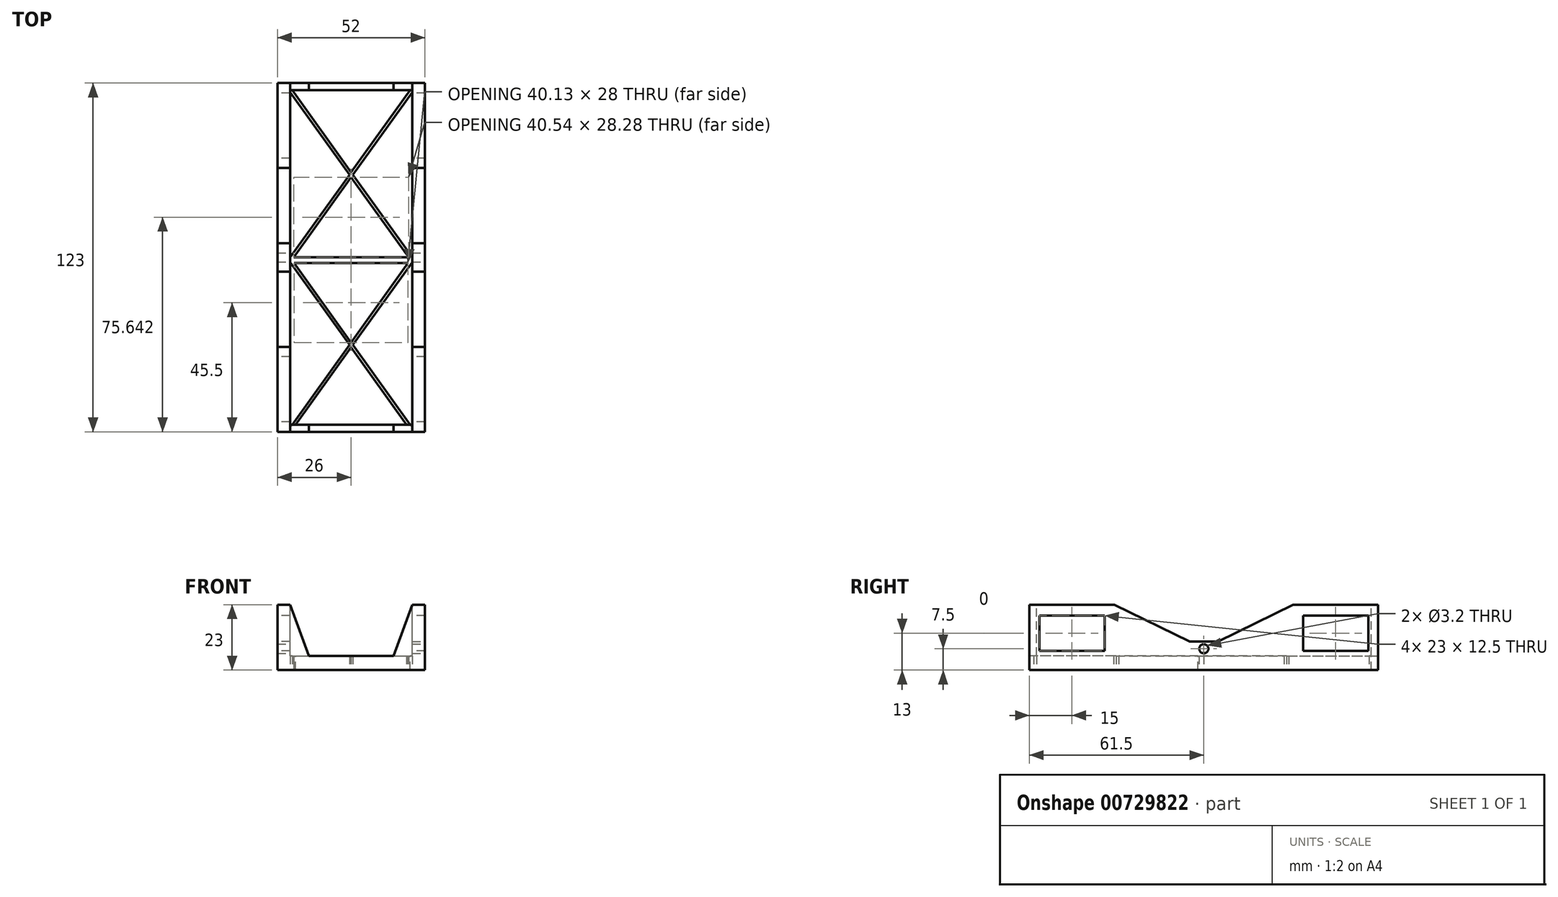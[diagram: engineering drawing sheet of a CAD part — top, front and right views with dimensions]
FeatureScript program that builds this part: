
annotation { "Feature Type Name" : "Feature", "Feature Type Description" : "" }
export const myFeature = defineFeature(function(context is Context, id is Id, definition is map)
    precondition{}
    {
        {
            var Q0;
            Q0=qCreatedBy(makeId("Top.planeOp"),FACE);
            var sketch = newSketch(context, id + "F0", { "sketchPlane" : qUnion([Q0])});
            skLineSegment(sketch, "E0.bottom", {"start": v(21.5, 60) * mm, "end": v(-21.5, 60) * mm});
            skLineSegment(sketch, "E0.top", {"start": v(21.5, -60) * mm, "end": v(-21.5, -60) * mm});
            skLineSegment(sketch, "E0.left", {"start": v(21.5, 60) * mm, "end": v(21.5, -60) * mm});
            skLineSegment(sketch, "E0.right", {"start": v(-21.5, 60) * mm, "end": v(-21.5, -60) * mm});
            skPoint(sketch, "E0.middle", {"position": v(0, 0) * mm});
            skLineSegment(sketch, "E1.bottom", {"start": v(23, 61.5) * mm, "end": v(-23, 61.5) * mm});
            skLineSegment(sketch, "E1.top", {"start": v(23, -61.5) * mm, "end": v(-23, -61.5) * mm});
            skLineSegment(sketch, "E1.left", {"start": v(23, 61.5) * mm, "end": v(23, -61.5) * mm});
            skLineSegment(sketch, "E1.right", {"start": v(-23, 61.5) * mm, "end": v(-23, -61.5) * mm});
            skLineSegment(sketch, "E2", {"start": v(-21.5, 0) * mm, "end": v(21.5, 60) * mm});
            skLineSegment(sketch, "E3", {"start": v(-21.5, 0) * mm, "end": v(21.5, -60) * mm});
            skLineSegment(sketch, "E4", {"start": v(-21.5, -60) * mm, "end": v(21.5, 0) * mm});
            skLineSegment(sketch, "E5", {"start": v(-21.5, 60) * mm, "end": v(21.5, 0) * mm});
            skLineSegment(sketch, "E6", {"start": v(-21.5, 0) * mm, "end": v(21.5, 0) * mm});
            skLineSegment(sketch, "E7.0", {"start": v(-22.31, -0.58) * mm, "end": v(20.69, -60.58) * mm});
            skLineSegment(sketch, "E8.0", {"start": v(-20.69, -60.58) * mm, "end": v(22.31, -0.58) * mm});
            skLineSegment(sketch, "E9.0", {"start": v(-21.5, -1) * mm, "end": v(21.5, -1) * mm});
            skLineSegment(sketch, "E10.0", {"start": v(-22.31, 59.42) * mm, "end": v(20.69, -0.58) * mm});
            skLineSegment(sketch, "E11.0", {"start": v(-20.69, -0.58) * mm, "end": v(22.31, 59.42) * mm});
            skSolve(sketch);
        }
        {
            var Q0;
            {var subQ2=sQuery(id+"F0.wireOp",EDGE,"E0.bottom");Q0=makeQuery(id+"F0.imprint","IMPRINT",FACE,{"disambiguationData":[TD([[makeQuery(id+"F0.imprint","IMPRINT",EDGE,{"derivedFrom":subQ2}),-1.0]])]});}
            var Q1;
            {var subQ1=sQuery(id+"F0.wireOp",EDGE,"E2");var subQ3=sQuery(id+"F0.wireOp",EDGE,"E10.0");var subQ4=makeQuery(id+"F0.imprint","INTERSECT",VERTEX,{"derivedFrom":[subQ1,subQ3]});Q1=makeQuery(id+"F0.imprint","IMPRINT",FACE,{"disambiguationData":[TD([[makeQuery(id+"F0.imprint","IMPRINT",EDGE,{"disambiguationData":[TD([[subQ4,-1.0]])],"derivedFrom":subQ3}),-1.0]])]});}
            var Q2;
            {var subQ0=sQuery(id+"F0.wireOp",EDGE,"E6");var subQ3=makeQuery(id+"F0.imprint","INTERSECT",VERTEX,{"derivedFrom":[subQ0,sQuery(id+"F0.wireOp",EDGE,"E11.0")]});Q2=makeQuery(id+"F0.imprint","IMPRINT",FACE,{"disambiguationData":[TD([[makeQuery(id+"F0.imprint","IMPRINT",EDGE,{"disambiguationData":[TD([[subQ3,-1.0]])],"derivedFrom":subQ0}),-1.0]])]});}
            var Q3;
            {var subQ1=sQuery(id+"F0.wireOp",EDGE,"E0.right");var subQ7=sQuery(id+"F0.wireOp",EDGE,"E9.0");var subQ9=makeQuery(id+"F0.imprint","INTERSECT",VERTEX,{"derivedFrom":[subQ1,subQ7]});Q3=makeQuery(id+"F0.imprint","IMPRINT",FACE,{"disambiguationData":[TD([[makeQuery(id+"F0.imprint","IMPRINT",EDGE,{"disambiguationData":[TD([[subQ9,-1.0]])],"derivedFrom":subQ1}),1.0]])]});}
            var Q4;
            {var subQ1=sQuery(id+"F0.wireOp",EDGE,"E0.left");var subQ5=sQuery(id+"F0.wireOp",EDGE,"E9.0");var subQ6=makeQuery(id+"F0.imprint","INTERSECT",VERTEX,{"derivedFrom":[subQ1,subQ5]});Q4=makeQuery(id+"F0.imprint","IMPRINT",FACE,{"disambiguationData":[TD([[makeQuery(id+"F0.imprint","IMPRINT",EDGE,{"disambiguationData":[TD([[subQ6,-1.0]])],"derivedFrom":subQ1}),-1.0]])]});}
            var Q5;
            {var subQ0=sQuery(id+"F0.wireOp",EDGE,"E4");var subQ5=sQuery(id+"F0.wireOp",EDGE,"E7.0");var subQ7=makeQuery(id+"F0.imprint","INTERSECT",VERTEX,{"derivedFrom":[subQ0,subQ5]});Q5=makeQuery(id+"F0.imprint","IMPRINT",FACE,{"disambiguationData":[TD([[makeQuery(id+"F0.imprint","IMPRINT",EDGE,{"disambiguationData":[TD([[subQ7,-1.0]])],"derivedFrom":subQ5}),-1.0]])]});}
            var Q6;
            {var subQ1=sQuery(id+"F0.wireOp",EDGE,"E0.top");var subQ3=sQuery(id+"F0.wireOp",EDGE,"E7.0");var subQ4=makeQuery(id+"F0.imprint","INTERSECT",VERTEX,{"derivedFrom":[subQ1,subQ3]});Q6=makeQuery(id+"F0.imprint","IMPRINT",FACE,{"disambiguationData":[TD([[makeQuery(id+"F0.imprint","IMPRINT",EDGE,{"disambiguationData":[TD([[subQ4,1.0]])],"derivedFrom":subQ3}),1.0]])]});}
            var Q7;
            {var subQ0=sQuery(id+"F0.wireOp",EDGE,"E4");var subQ1=sQuery(id+"F0.wireOp",EDGE,"E3");var subQ2=makeQuery(id+"F0.imprint","INTERSECT",VERTEX,{"derivedFrom":[subQ1,subQ0]});Q7=makeQuery(id+"F0.imprint","IMPRINT",FACE,{"disambiguationData":[TD([[makeQuery(id+"F0.imprint","IMPRINT",EDGE,{"disambiguationData":[TD([[subQ2,-1.0]])],"derivedFrom":subQ1}),-1.0]])]});}
            var Q8;
            {var subQ0=sQuery(id+"F0.wireOp",EDGE,"E6");var subQ5=sQuery(id+"F0.wireOp",EDGE,"E10.0");var subQ6=makeQuery(id+"F0.imprint","INTERSECT",VERTEX,{"derivedFrom":[subQ0,subQ5]});Q8=makeQuery(id+"F0.imprint","IMPRINT",FACE,{"disambiguationData":[TD([[makeQuery(id+"F0.imprint","IMPRINT",EDGE,{"disambiguationData":[TD([[subQ6,1.0]])],"derivedFrom":subQ5}),1.0]])]});}
            var Q9;
            {var subQ1=sQuery(id+"F0.wireOp",EDGE,"E0.left");var subQ3=sQuery(id+"F0.wireOp",EDGE,"E9.0");var subQ4=makeQuery(id+"F0.imprint","INTERSECT",VERTEX,{"derivedFrom":[subQ1,subQ3]});Q9=makeQuery(id+"F0.imprint","IMPRINT",FACE,{"disambiguationData":[TD([[makeQuery(id+"F0.imprint","IMPRINT",EDGE,{"disambiguationData":[TD([[subQ4,1.0]])],"derivedFrom":subQ3}),1.0]])]});}
            var Q10;
            {var subQ1=sQuery(id+"F0.wireOp",EDGE,"E0.right");var subQ3=sQuery(id+"F0.wireOp",EDGE,"E9.0");var subQ4=makeQuery(id+"F0.imprint","INTERSECT",VERTEX,{"derivedFrom":[subQ1,subQ3]});Q10=makeQuery(id+"F0.imprint","IMPRINT",FACE,{"disambiguationData":[TD([[makeQuery(id+"F0.imprint","IMPRINT",EDGE,{"disambiguationData":[TD([[subQ4,-1.0]])],"derivedFrom":subQ3}),1.0]])]});}
            var Q11;
            {var subQ0=sQuery(id+"F0.wireOp",EDGE,"E10.0");var subQ1=sQuery(id+"F0.wireOp",EDGE,"E2");var subQ2=makeQuery(id+"F0.imprint","INTERSECT",VERTEX,{"derivedFrom":[subQ1,subQ0]});Q11=makeQuery(id+"F0.imprint","IMPRINT",FACE,{"disambiguationData":[TD([[makeQuery(id+"F0.imprint","IMPRINT",EDGE,{"disambiguationData":[TD([[subQ2,-1.0]])],"derivedFrom":subQ1}),-1.0]])]});}
            var Q12;
            {var subQ0=sQuery(id+"F0.wireOp",EDGE,"E2");var subQ5=sQuery(id+"F0.wireOp",EDGE,"E5");var subQ7=makeQuery(id+"F0.imprint","INTERSECT",VERTEX,{"derivedFrom":[subQ0,subQ5]});Q12=makeQuery(id+"F0.imprint","IMPRINT",FACE,{"disambiguationData":[TD([[makeQuery(id+"F0.imprint","IMPRINT",EDGE,{"disambiguationData":[TD([[subQ7,-1.0]])],"derivedFrom":subQ5}),1.0]])]});}
            var Q13;
            {var subQ3=sQuery(id+"F0.wireOp",EDGE,"E10.0");var subQ5=sQuery(id+"F0.wireOp",EDGE,"E2");var subQ6=makeQuery(id+"F0.imprint","INTERSECT",VERTEX,{"derivedFrom":[subQ5,subQ3]});Q13=makeQuery(id+"F0.imprint","IMPRINT",FACE,{"disambiguationData":[TD([[makeQuery(id+"F0.imprint","IMPRINT",EDGE,{"disambiguationData":[TD([[subQ6,-1.0]])],"derivedFrom":subQ5}),1.0]])]});}
            extrude(context, id + "F1", {"entities" : qUnion([Q0, Q1, Q2, Q3, Q4, Q5, Q6, Q7, Q8, Q9, Q10, Q11, Q12, Q13]), "depth" : 5 * mm, "offsetDistance" : 25 * mm});
        }
        {
            var Q0;
            Q0=makeQuery(id+"F1.opExtrude","SWEPT_FACE",FACE,{"disambiguationData":[OSD([sQuery(id+"F0.wireOp",EDGE,"E1.right")])]});
            var sketch = newSketch(context, id + "F2", { "sketchPlane" : qUnion([Q0])});
            skLineSegment(sketch, "E12.bottom", {"start": v(-61.5, 5) * mm, "end": v(-31.5, 5) * mm});
            skLineSegment(sketch, "E12.top", {"start": v(-61.5, 23) * mm, "end": v(-31.5, 23) * mm});
            skLineSegment(sketch, "E12.left", {"start": v(-61.5, 5) * mm, "end": v(-61.5, 23) * mm});
            skLineSegment(sketch, "E12.right", {"start": v(-31.5, 5) * mm, "end": v(-31.5, 23) * mm});
            skLineSegment(sketch, "E13.bottom", {"start": v(61.5, 5) * mm, "end": v(31.5, 5) * mm});
            skLineSegment(sketch, "E13.top", {"start": v(61.5, 23) * mm, "end": v(31.5, 23) * mm});
            skLineSegment(sketch, "E13.left", {"start": v(61.5, 5) * mm, "end": v(61.5, 23) * mm});
            skLineSegment(sketch, "E13.right", {"start": v(31.5, 5) * mm, "end": v(31.5, 23) * mm});
            skSolve(sketch);
        }
        {
            var Q0;
            Q0 = qSketchRegion(id + "F2", true);
            extrude(context, id + "F3", {"entities" : qUnion([Q0]), "operationType" : NewBodyOperationType.ADD, "oppositeDirection" : true, "depth" : 46 * mm, "offsetDistance" : 25 * mm});
        }
        {
            var Q0;
            Q0=makeQuery(id+"F3.opExtrude","SWEPT_FACE",FACE,{"disambiguationData":[OSD([sQuery(id+"F2.wireOp",EDGE,"E12.top")])]});
            var sketch = newSketch(context, id + "F4", { "sketchPlane" : qUnion([Q0])});
            skLineSegment(sketch, "E14.bottom", {"start": v(-21.5, 61.5) * mm, "end": v(21.5, 61.5) * mm});
            skLineSegment(sketch, "E14.top", {"start": v(-21.5, 31.5) * mm, "end": v(21.5, 31.5) * mm});
            skLineSegment(sketch, "E14.left", {"start": v(-21.5, 61.5) * mm, "end": v(-21.5, 31.5) * mm});
            skLineSegment(sketch, "E14.right", {"start": v(21.5, 61.5) * mm, "end": v(21.5, 31.5) * mm});
            skLineSegment(sketch, "E15.bottom", {"start": v(-21.5, -61.5) * mm, "end": v(21.5, -61.5) * mm});
            skLineSegment(sketch, "E15.top", {"start": v(-21.5, -31.5) * mm, "end": v(21.5, -31.5) * mm});
            skLineSegment(sketch, "E15.left", {"start": v(-21.5, -61.5) * mm, "end": v(-21.5, -31.5) * mm});
            skLineSegment(sketch, "E15.right", {"start": v(21.5, -61.5) * mm, "end": v(21.5, -31.5) * mm});
            skSolve(sketch);
        }
        {
            var Q0;
            Q0 = qSketchRegion(id + "F4", true);
            extrude(context, id + "F5", {"entities" : qUnion([Q0]), "operationType" : NewBodyOperationType.REMOVE, "oppositeDirection" : true, "depth" : 18 * mm, "offsetDistance" : 25 * mm});
        }
        {
            var Q0;
            Q0=makeQuery(id+"F3.boolean.opBoolean","MERGE",FACE,{"derivedFrom":[makeQuery(id+"F1.opExtrude","SWEPT_FACE",FACE,{"disambiguationData":[OSD([sQuery(id+"F0.wireOp",EDGE,"E1.right")])]}),makeQuery(id+"F3.opExtrude","CAP_FACE",FACE,{"disambiguationData":[OSD([sQuery(id+"F2.wireOp",EDGE,"E12.bottom"),sQuery(id+"F2.wireOp",EDGE,"E12.top"),sQuery(id+"F2.wireOp",EDGE,"E12.left"),sQuery(id+"F2.wireOp",EDGE,"E12.right")])],"isStart":true}),makeQuery(id+"F3.opExtrude","CAP_FACE",FACE,{"disambiguationData":[OSD([sQuery(id+"F2.wireOp",EDGE,"E13.bottom"),sQuery(id+"F2.wireOp",EDGE,"E13.top"),sQuery(id+"F2.wireOp",EDGE,"E13.left"),sQuery(id+"F2.wireOp",EDGE,"E13.right")])],"isStart":true})]});
            var sketch = newSketch(context, id + "F6", { "sketchPlane" : qUnion([Q0])});
            skLineSegment(sketch, "E16.bottom", {"start": v(-58, 19.25) * mm, "end": v(-35, 19.25) * mm});
            skLineSegment(sketch, "E16.top", {"start": v(-58, 6.75) * mm, "end": v(-35, 6.75) * mm});
            skLineSegment(sketch, "E16.left", {"start": v(-58, 19.25) * mm, "end": v(-58, 6.75) * mm});
            skLineSegment(sketch, "E16.right", {"start": v(-35, 19.25) * mm, "end": v(-35, 6.75) * mm});
            skLineSegment(sketch, "E17.bottom", {"start": v(35, 19.25) * mm, "end": v(58, 19.25) * mm});
            skLineSegment(sketch, "E17.top", {"start": v(35, 6.75) * mm, "end": v(58, 6.75) * mm});
            skLineSegment(sketch, "E17.left", {"start": v(35, 19.25) * mm, "end": v(35, 6.75) * mm});
            skLineSegment(sketch, "E17.right", {"start": v(58, 19.25) * mm, "end": v(58, 6.75) * mm});
            skSolve(sketch);
        }
        {
            var Q0;
            Q0 = qSketchRegion(id + "F6", true);
            extrude(context, id + "F7", {"entities" : qUnion([Q0]), "operationType" : NewBodyOperationType.REMOVE, "endBound" : BoundingType.THROUGH_ALL, "oppositeDirection" : true, "depth" : 25 * mm, "offsetDistance" : 25 * mm});
        }
        {
            var Q0;
            Q0=makeQuery(id+"F3.boolean.opBoolean","MERGE",FACE,{"derivedFrom":[makeQuery(id+"F1.opExtrude","SWEPT_FACE",FACE,{"disambiguationData":[OSD([sQuery(id+"F0.wireOp",EDGE,"E1.right")])]}),makeQuery(id+"F3.opExtrude","CAP_FACE",FACE,{"disambiguationData":[OSD([sQuery(id+"F2.wireOp",EDGE,"E12.bottom"),sQuery(id+"F2.wireOp",EDGE,"E12.top"),sQuery(id+"F2.wireOp",EDGE,"E12.left"),sQuery(id+"F2.wireOp",EDGE,"E12.right")])],"isStart":true}),makeQuery(id+"F3.opExtrude","CAP_FACE",FACE,{"disambiguationData":[OSD([sQuery(id+"F2.wireOp",EDGE,"E13.bottom"),sQuery(id+"F2.wireOp",EDGE,"E13.top"),sQuery(id+"F2.wireOp",EDGE,"E13.left"),sQuery(id+"F2.wireOp",EDGE,"E13.right")])],"isStart":true})]});
            extrude(context, id + "F8", {"entities" : qUnion([Q0]), "operationType" : NewBodyOperationType.ADD, "depth" : 1 * mm, "offsetDistance" : 25 * mm});
        }
        {
            var Q0;
            Q0=makeQuery(id+"F3.boolean.opBoolean","MERGE",FACE,{"derivedFrom":[makeQuery(id+"F1.opExtrude","SWEPT_FACE",FACE,{"disambiguationData":[OSD([sQuery(id+"F0.wireOp",EDGE,"E1.left")])]}),makeQuery(id+"F3.opExtrude","CAP_FACE",FACE,{"disambiguationData":[OSD([sQuery(id+"F2.wireOp",EDGE,"E12.bottom"),sQuery(id+"F2.wireOp",EDGE,"E12.top"),sQuery(id+"F2.wireOp",EDGE,"E12.left"),sQuery(id+"F2.wireOp",EDGE,"E12.right")])],"isStart":false}),makeQuery(id+"F3.opExtrude","CAP_FACE",FACE,{"disambiguationData":[OSD([sQuery(id+"F2.wireOp",EDGE,"E13.bottom"),sQuery(id+"F2.wireOp",EDGE,"E13.top"),sQuery(id+"F2.wireOp",EDGE,"E13.left"),sQuery(id+"F2.wireOp",EDGE,"E13.right")])],"isStart":false})]});
            extrude(context, id + "F9", {"entities" : qUnion([Q0]), "operationType" : NewBodyOperationType.ADD, "depth" : 1 * mm, "offsetDistance" : 25 * mm});
        }
        {
            var Q0;
            Q0=makeQuery(id+"F8.opExtrude","CAP_FACE",FACE,{"disambiguationData":[OSD([sQuery(id+"F0.wireOp",EDGE,"E1.right"),sQuery(id+"F2.wireOp",EDGE,"E12.bottom"),sQuery(id+"F2.wireOp",EDGE,"E12.top"),sQuery(id+"F2.wireOp",EDGE,"E12.left"),sQuery(id+"F2.wireOp",EDGE,"E12.right"),sQuery(id+"F2.wireOp",EDGE,"E13.bottom"),sQuery(id+"F2.wireOp",EDGE,"E13.top"),sQuery(id+"F2.wireOp",EDGE,"E13.left"),sQuery(id+"F2.wireOp",EDGE,"E13.right")])],"isStart":false});
            var sketch = newSketch(context, id + "F10", { "sketchPlane" : qUnion([Q0])});
            skLineSegment(sketch, "E18.bottom", {"start": v(5, 0) * mm, "end": v(-5, 0) * mm});
            skLineSegment(sketch, "E18.top", {"start": v(5, 10) * mm, "end": v(-5, 10) * mm});
            skLineSegment(sketch, "E18.left", {"start": v(5, 0) * mm, "end": v(5, 10) * mm});
            skLineSegment(sketch, "E18.right", {"start": v(-5, 0) * mm, "end": v(-5, 10) * mm});
            skPoint(sketch, "E18.middle", {"position": v(0, 5) * mm});
            skSolve(sketch);
        }
        {
            var Q0;
            Q0 = qSketchRegion(id + "F10", true);
            extrude(context, id + "F11", {"entities" : qUnion([Q0]), "operationType" : NewBodyOperationType.ADD, "oppositeDirection" : true, "depth" : 2.5 * mm, "offsetDistance" : 25 * mm});
        }
        {
            var Q0;
            Q0=makeQuery(id+"F9.opExtrude","CAP_FACE",FACE,{"disambiguationData":[OSD([sQuery(id+"F0.wireOp",EDGE,"E1.left"),sQuery(id+"F2.wireOp",EDGE,"E12.bottom"),sQuery(id+"F2.wireOp",EDGE,"E12.top"),sQuery(id+"F2.wireOp",EDGE,"E12.left"),sQuery(id+"F2.wireOp",EDGE,"E12.right"),sQuery(id+"F2.wireOp",EDGE,"E13.bottom"),sQuery(id+"F2.wireOp",EDGE,"E13.top"),sQuery(id+"F2.wireOp",EDGE,"E13.left"),sQuery(id+"F2.wireOp",EDGE,"E13.right")])],"isStart":false});
            var sketch = newSketch(context, id + "F12", { "sketchPlane" : qUnion([Q0])});
            skLineSegment(sketch, "E19.bottom", {"start": v(-5, 0) * mm, "end": v(5, 0) * mm});
            skLineSegment(sketch, "E19.top", {"start": v(-5, 10) * mm, "end": v(5, 10) * mm});
            skLineSegment(sketch, "E19.left", {"start": v(-5, 0) * mm, "end": v(-5, 10) * mm});
            skLineSegment(sketch, "E19.right", {"start": v(5, 0) * mm, "end": v(5, 10) * mm});
            skPoint(sketch, "E19.middle", {"position": v(0, 5) * mm});
            skSolve(sketch);
        }
        {
            var Q0;
            Q0 = qSketchRegion(id + "F12", true);
            extrude(context, id + "F13", {"entities" : qUnion([Q0]), "operationType" : NewBodyOperationType.ADD, "oppositeDirection" : true, "depth" : 2.5 * mm, "offsetDistance" : 25 * mm});
        }
        {
            var Q0;
            Q0=makeQuery(id+"F13.boolean.opBoolean","MERGE",FACE,{"derivedFrom":[makeQuery(id+"F9.opExtrude","CAP_FACE",FACE,{"disambiguationData":[OSD([sQuery(id+"F0.wireOp",EDGE,"E1.left"),sQuery(id+"F2.wireOp",EDGE,"E12.bottom"),sQuery(id+"F2.wireOp",EDGE,"E12.top"),sQuery(id+"F2.wireOp",EDGE,"E12.left"),sQuery(id+"F2.wireOp",EDGE,"E12.right"),sQuery(id+"F2.wireOp",EDGE,"E13.bottom"),sQuery(id+"F2.wireOp",EDGE,"E13.top"),sQuery(id+"F2.wireOp",EDGE,"E13.left"),sQuery(id+"F2.wireOp",EDGE,"E13.right")])],"isStart":false}),makeQuery(id+"F13.opExtrude","CAP_FACE",FACE,{"disambiguationData":[OSD([sQuery(id+"F12.wireOp",EDGE,"E19.bottom"),sQuery(id+"F12.wireOp",EDGE,"E19.top"),sQuery(id+"F12.wireOp",EDGE,"E19.left"),sQuery(id+"F12.wireOp",EDGE,"E19.right")])],"isStart":true})]});
            var sketch = newSketch(context, id + "F14", { "sketchPlane" : qUnion([Q0])});
            skCircle(sketch, "E20", {"center": v(0, 7.5) * mm, "radius": 1.6 * mm});
            skPoint(sketch, "E20.centerSnap0", {"position": v(-5, 7.5) * mm});
            skPoint(sketch, "E20.centerSnap1", {"position": v(0, 10) * mm});
            skSolve(sketch);
        }
        {
            var Q0;
            Q0 = qSketchRegion(id + "F14", true);
            extrude(context, id + "F15", {"entities" : qUnion([Q0]), "operationType" : NewBodyOperationType.REMOVE, "endBound" : BoundingType.THROUGH_ALL, "oppositeDirection" : true, "depth" : 25 * mm, "offsetDistance" : 25 * mm});
        }
        {
            var Q0;
            Q0=makeQuery(id+"F13.boolean.opBoolean","MERGE",FACE,{"derivedFrom":[makeQuery(id+"F9.opExtrude","CAP_FACE",FACE,{"disambiguationData":[OSD([sQuery(id+"F0.wireOp",EDGE,"E1.left"),sQuery(id+"F2.wireOp",EDGE,"E12.bottom"),sQuery(id+"F2.wireOp",EDGE,"E12.top"),sQuery(id+"F2.wireOp",EDGE,"E12.left"),sQuery(id+"F2.wireOp",EDGE,"E12.right"),sQuery(id+"F2.wireOp",EDGE,"E13.bottom"),sQuery(id+"F2.wireOp",EDGE,"E13.top"),sQuery(id+"F2.wireOp",EDGE,"E13.left"),sQuery(id+"F2.wireOp",EDGE,"E13.right")])],"isStart":false}),makeQuery(id+"F13.opExtrude","CAP_FACE",FACE,{"disambiguationData":[OSD([sQuery(id+"F12.wireOp",EDGE,"E19.bottom"),sQuery(id+"F12.wireOp",EDGE,"E19.top"),sQuery(id+"F12.wireOp",EDGE,"E19.left"),sQuery(id+"F12.wireOp",EDGE,"E19.right")])],"isStart":true})]});
            extrude(context, id + "F16", {"entities" : qUnion([Q0]), "operationType" : NewBodyOperationType.ADD, "depth" : 2 * mm, "offsetDistance" : 25 * mm});
        }
        {
            var Q0;
            Q0=makeQuery(id+"F10.imprint","IMPRINT",FACE,{"disambiguationData":[TD([[makeQuery(id+"F10.imprint","IMPRINT",EDGE,{"derivedFrom":makeQuery(id+"F8.opExtrude","CAP_EDGE",EDGE,{"disambiguationData":[OSD([sQuery(id+"F2.wireOp",EDGE,"E12.top")])],"isStart":false})}),-1.0]])]});
            var Q1;
            Q1=makeQuery(id+"F11.boolean.opBoolean","MERGE",FACE,{"derivedFrom":[makeQuery(id+"F8.opExtrude","CAP_FACE",FACE,{"disambiguationData":[OSD([sQuery(id+"F0.wireOp",EDGE,"E1.right"),sQuery(id+"F2.wireOp",EDGE,"E12.bottom"),sQuery(id+"F2.wireOp",EDGE,"E12.top"),sQuery(id+"F2.wireOp",EDGE,"E12.left"),sQuery(id+"F2.wireOp",EDGE,"E12.right"),sQuery(id+"F2.wireOp",EDGE,"E13.bottom"),sQuery(id+"F2.wireOp",EDGE,"E13.top"),sQuery(id+"F2.wireOp",EDGE,"E13.left"),sQuery(id+"F2.wireOp",EDGE,"E13.right")])],"isStart":false}),makeQuery(id+"F11.opExtrude","CAP_FACE",FACE,{"disambiguationData":[OSD([sQuery(id+"F10.wireOp",EDGE,"E18.bottom"),sQuery(id+"F10.wireOp",EDGE,"E18.top"),sQuery(id+"F10.wireOp",EDGE,"E18.left"),sQuery(id+"F10.wireOp",EDGE,"E18.right")])],"isStart":true})]});
            extrude(context, id + "F17", {"entities" : qUnion([Q0, Q1]), "operationType" : NewBodyOperationType.ADD, "depth" : 2 * mm, "offsetDistance" : 25 * mm});
        }
        {
            var Q0;
            Q0=makeQuery(id+"F1.opExtrude","SWEPT_FACE",FACE,{"disambiguationData":[OSD([sQuery(id+"F0.wireOp",EDGE,"E0.bottom")])]});
            extrude(context, id + "F18", {"entities" : qUnion([Q0]), "operationType" : NewBodyOperationType.ADD, "depth" : 1 * mm, "offsetDistance" : 25 * mm});
        }
        {
            var Q0;
            Q0=makeQuery(id+"F1.opExtrude","SWEPT_FACE",FACE,{"disambiguationData":[OSD([sQuery(id+"F0.wireOp",EDGE,"E0.top")])]});
            extrude(context, id + "F19", {"entities" : qUnion([Q0]), "operationType" : NewBodyOperationType.ADD, "depth" : 1 * mm, "offsetDistance" : 25 * mm});
        }
        {
            var Q0;
            Q0=makeQuery(id+"F1.opExtrude","SWEPT_FACE",FACE,{"disambiguationData":[OSD([sQuery(id+"F0.wireOp",EDGE,"E9.0")])]});
            extrude(context, id + "F20", {"entities" : qUnion([Q0]), "operationType" : NewBodyOperationType.ADD, "depth" : 1 * mm, "offsetDistance" : 25 * mm});
        }
        {
            var Q0;
            {var subQ0=sQuery(id+"F2.wireOp",EDGE,"E12.left");var subQ1=sQuery(id+"F0.wireOp",EDGE,"E1.right");var subQ2=sQuery(id+"F0.wireOp",EDGE,"E1.bottom");var subQ3=sQuery(id+"F0.wireOp",EDGE,"E1.left");Q0=makeQuery(id+"F17.boolean.opBoolean","MERGE",FACE,{"derivedFrom":[makeQuery(id+"F16.boolean.opBoolean","MERGE",FACE,{"derivedFrom":[makeQuery(id+"F9.boolean.opBoolean","MERGE",FACE,{"derivedFrom":[makeQuery(id+"F8.boolean.opBoolean","MERGE",FACE,{"derivedFrom":[makeQuery(id+"F3.boolean.opBoolean","MERGE",FACE,{"derivedFrom":[makeQuery(id+"F1.opExtrude","SWEPT_FACE",FACE,{"disambiguationData":[OSD([subQ2])]}),makeQuery(id+"F3.opExtrude","SWEPT_FACE",FACE,{"disambiguationData":[OSD([subQ0])]})]}),makeQuery(id+"F8.opExtrude","SWEPT_FACE",FACE,{"disambiguationData":[OSD([subQ2,subQ1,subQ0])]})]}),makeQuery(id+"F9.opExtrude","SWEPT_FACE",FACE,{"disambiguationData":[OSD([subQ2,subQ3,subQ0])]})]}),makeQuery(id+"F16.opExtrude","SWEPT_FACE",FACE,{"disambiguationData":[OSD([subQ2,subQ3,subQ0])]})]}),makeQuery(id+"F17.opExtrude","SWEPT_FACE",FACE,{"disambiguationData":[OSD([subQ2,subQ1,subQ0]),TDD([makeQuery(id+"F10.imprint","IMPRINT",EDGE,{"derivedFrom":makeQuery(id+"F8.opExtrude","CAP_EDGE",EDGE,{"disambiguationData":[OSD([subQ2,subQ1,subQ0])],"isStart":false})})])]})]});}
            var sketch = newSketch(context, id + "F21", { "sketchPlane" : qUnion([Q0])});
            skLineSegment(sketch, "E21", {"start": v(-21.5, 5) * mm, "end": v(-21.5, 23) * mm});
            skLineSegment(sketch, "E22", {"start": v(-21.5, 23) * mm, "end": v(-14.95, 5) * mm});
            skLineSegment(sketch, "E23", {"start": v(21.5, 23) * mm, "end": v(21.5, 5) * mm});
            skLineSegment(sketch, "E24", {"start": v(21.5, 5) * mm, "end": v(14.95, 5) * mm});
            skLineSegment(sketch, "E25", {"start": v(14.95, 5) * mm, "end": v(21.5, 23) * mm});
            skSolve(sketch);
        }
        {
            var Q0;
            {var subQ0=sQuery(id+"F21.wireOp",EDGE,"E21");Q0=makeQuery(id+"F21.imprint","IMPRINT",FACE,{"disambiguationData":[TD([[makeQuery(id+"F21.imprint","IMPRINT",EDGE,{"derivedFrom":subQ0}),-1.0]])]});}
            var Q1;
            Q1=makeQuery(id+"F21.imprint","IMPRINT",FACE,{"disambiguationData":[TD([[makeQuery(id+"F21.imprint","IMPRINT",EDGE,{"derivedFrom":sQuery(id+"F21.wireOp",EDGE,"E23")}),1.0]])]});
            extrude(context, id + "F22", {"entities" : qUnion([Q0, Q1]), "operationType" : NewBodyOperationType.ADD, "oppositeDirection" : true, "depth" : 2.5 * mm, "offsetDistance" : 25 * mm});
        }
        {
            var Q0;
            {var subQ0=sQuery(id+"F2.wireOp",EDGE,"E13.left");var subQ1=sQuery(id+"F0.wireOp",EDGE,"E1.right");var subQ2=sQuery(id+"F0.wireOp",EDGE,"E1.top");var subQ3=sQuery(id+"F0.wireOp",EDGE,"E1.left");Q0=makeQuery(id+"F17.boolean.opBoolean","MERGE",FACE,{"derivedFrom":[makeQuery(id+"F16.boolean.opBoolean","MERGE",FACE,{"derivedFrom":[makeQuery(id+"F9.boolean.opBoolean","MERGE",FACE,{"derivedFrom":[makeQuery(id+"F8.boolean.opBoolean","MERGE",FACE,{"derivedFrom":[makeQuery(id+"F3.boolean.opBoolean","MERGE",FACE,{"derivedFrom":[makeQuery(id+"F1.opExtrude","SWEPT_FACE",FACE,{"disambiguationData":[OSD([subQ2])]}),makeQuery(id+"F3.opExtrude","SWEPT_FACE",FACE,{"disambiguationData":[OSD([subQ0])]})]}),makeQuery(id+"F8.opExtrude","SWEPT_FACE",FACE,{"disambiguationData":[OSD([subQ2,subQ1,subQ0])]})]}),makeQuery(id+"F9.opExtrude","SWEPT_FACE",FACE,{"disambiguationData":[OSD([subQ2,subQ3,subQ0])]})]}),makeQuery(id+"F16.opExtrude","SWEPT_FACE",FACE,{"disambiguationData":[OSD([subQ2,subQ3,subQ0])]})]}),makeQuery(id+"F17.opExtrude","SWEPT_FACE",FACE,{"disambiguationData":[OSD([subQ2,subQ1,subQ0])]})]});}
            var sketch = newSketch(context, id + "F23", { "sketchPlane" : qUnion([Q0])});
            skLineSegment(sketch, "E26", {"start": v(-21.5, 23) * mm, "end": v(-14.95, 5) * mm});
            skLineSegment(sketch, "E27", {"start": v(21.5, 23) * mm, "end": v(14.95, 5) * mm});
            skSolve(sketch);
        }
        {
            var Q0;
            {var subQ0=sQuery(id+"F23.wireOp",EDGE,"E27");Q0=makeQuery(id+"F23.imprint","IMPRINT",FACE,{"disambiguationData":[TD([[makeQuery(id+"F23.imprint","IMPRINT",EDGE,{"derivedFrom":subQ0}),1.0]])]});}
            var Q1;
            {var subQ0=sQuery(id+"F23.wireOp",EDGE,"E26");Q1=makeQuery(id+"F23.imprint","IMPRINT",FACE,{"disambiguationData":[TD([[makeQuery(id+"F23.imprint","IMPRINT",EDGE,{"derivedFrom":subQ0}),-1.0]])]});}
            extrude(context, id + "F24", {"entities" : qUnion([Q0, Q1]), "operationType" : NewBodyOperationType.ADD, "oppositeDirection" : true, "depth" : 2.5 * mm, "offsetDistance" : 25 * mm});
        }
        {
            var Q0;
            {var subQ0=sQuery(id+"F10.wireOp",EDGE,"E18.right");var subQ1=sQuery(id+"F2.wireOp",EDGE,"E12.right");var subQ2=sQuery(id+"F2.wireOp",EDGE,"E12.left");var subQ3=sQuery(id+"F2.wireOp",EDGE,"E12.top");var subQ4=sQuery(id+"F0.wireOp",EDGE,"E1.right");Q0=makeQuery(id+"F17.boolean.opBoolean","MERGE",FACE,{"derivedFrom":[makeQuery(id+"F17.opExtrude","CAP_FACE",FACE,{"disambiguationData":[OSD([sQuery(id+"F0.wireOp",EDGE,"E1.bottom"),subQ4,subQ3,subQ2,subQ1,sQuery(id+"F6.wireOp",EDGE,"E16.bottom"),sQuery(id+"F6.wireOp",EDGE,"E16.top"),sQuery(id+"F6.wireOp",EDGE,"E16.left"),sQuery(id+"F6.wireOp",EDGE,"E16.right"),subQ0])],"isStart":false}),makeQuery(id+"F17.opExtrude","CAP_FACE",FACE,{"disambiguationData":[OSD([subQ4,sQuery(id+"F2.wireOp",EDGE,"E12.bottom"),subQ3,subQ2,subQ1,sQuery(id+"F2.wireOp",EDGE,"E13.bottom"),sQuery(id+"F2.wireOp",EDGE,"E13.top"),sQuery(id+"F2.wireOp",EDGE,"E13.left"),sQuery(id+"F2.wireOp",EDGE,"E13.right"),sQuery(id+"F10.wireOp",EDGE,"E18.bottom"),sQuery(id+"F10.wireOp",EDGE,"E18.top"),sQuery(id+"F10.wireOp",EDGE,"E18.left"),subQ0])],"isStart":false})]});}
            var sketch = newSketch(context, id + "F25", { "sketchPlane" : qUnion([Q0])});
            skLineSegment(sketch, "E28", {"start": v(-31.5, 23) * mm, "end": v(-5, 10) * mm});
            skLineSegment(sketch, "E29", {"start": v(5, 10) * mm, "end": v(31.5, 23) * mm});
            skSolve(sketch);
        }
        {
            var Q0;
            Q0=makeQuery(id+"F25.imprint","IMPRINT",FACE,{"disambiguationData":[TD([[makeQuery(id+"F25.imprint","IMPRINT",EDGE,{"derivedFrom":sQuery(id+"F25.wireOp",EDGE,"E28")}),-1.0]])]});
            var Q1;
            Q1=makeQuery(id+"F25.imprint","IMPRINT",FACE,{"disambiguationData":[TD([[makeQuery(id+"F25.imprint","IMPRINT",EDGE,{"derivedFrom":sQuery(id+"F25.wireOp",EDGE,"E29")}),-1.0]])]});
            extrude(context, id + "F26", {"entities" : qUnion([Q0, Q1]), "operationType" : NewBodyOperationType.ADD, "oppositeDirection" : true, "depth" : 4.5 * mm, "offsetDistance" : 25 * mm});
        }
        {
            var Q0;
            Q0=makeQuery(id+"F16.opExtrude","CAP_FACE",FACE,{"disambiguationData":[OSD([sQuery(id+"F0.wireOp",EDGE,"E1.left"),sQuery(id+"F2.wireOp",EDGE,"E12.bottom"),sQuery(id+"F2.wireOp",EDGE,"E12.top"),sQuery(id+"F2.wireOp",EDGE,"E12.left"),sQuery(id+"F2.wireOp",EDGE,"E12.right"),sQuery(id+"F2.wireOp",EDGE,"E13.bottom"),sQuery(id+"F2.wireOp",EDGE,"E13.top"),sQuery(id+"F2.wireOp",EDGE,"E13.left"),sQuery(id+"F2.wireOp",EDGE,"E13.right"),sQuery(id+"F12.wireOp",EDGE,"E19.bottom"),sQuery(id+"F12.wireOp",EDGE,"E19.top"),sQuery(id+"F12.wireOp",EDGE,"E19.left"),sQuery(id+"F12.wireOp",EDGE,"E19.right")])],"isStart":false});
            var sketch = newSketch(context, id + "F27", { "sketchPlane" : qUnion([Q0])});
            skLineSegment(sketch, "E30", {"start": v(31.5, 23) * mm, "end": v(5, 10) * mm});
            skLineSegment(sketch, "E31", {"start": v(5, 10) * mm, "end": v(-5, 10) * mm});
            skLineSegment(sketch, "E32", {"start": v(-5, 10) * mm, "end": v(-31.5, 23) * mm});
            skSolve(sketch);
        }
        {
            var Q0;
            Q0=makeQuery(id+"F27.imprint","IMPRINT",FACE,{"disambiguationData":[TD([[makeQuery(id+"F27.imprint","IMPRINT",EDGE,{"derivedFrom":sQuery(id+"F27.wireOp",EDGE,"E30")}),1.0]])]});
            var Q1;
            Q1=makeQuery(id+"F27.imprint","IMPRINT",FACE,{"disambiguationData":[TD([[makeQuery(id+"F27.imprint","IMPRINT",EDGE,{"derivedFrom":sQuery(id+"F27.wireOp",EDGE,"E32")}),1.0]])]});
            extrude(context, id + "F28", {"entities" : qUnion([Q0, Q1]), "operationType" : NewBodyOperationType.ADD, "oppositeDirection" : true, "depth" : 4.5 * mm, "offsetDistance" : 25 * mm});
        }
    });
